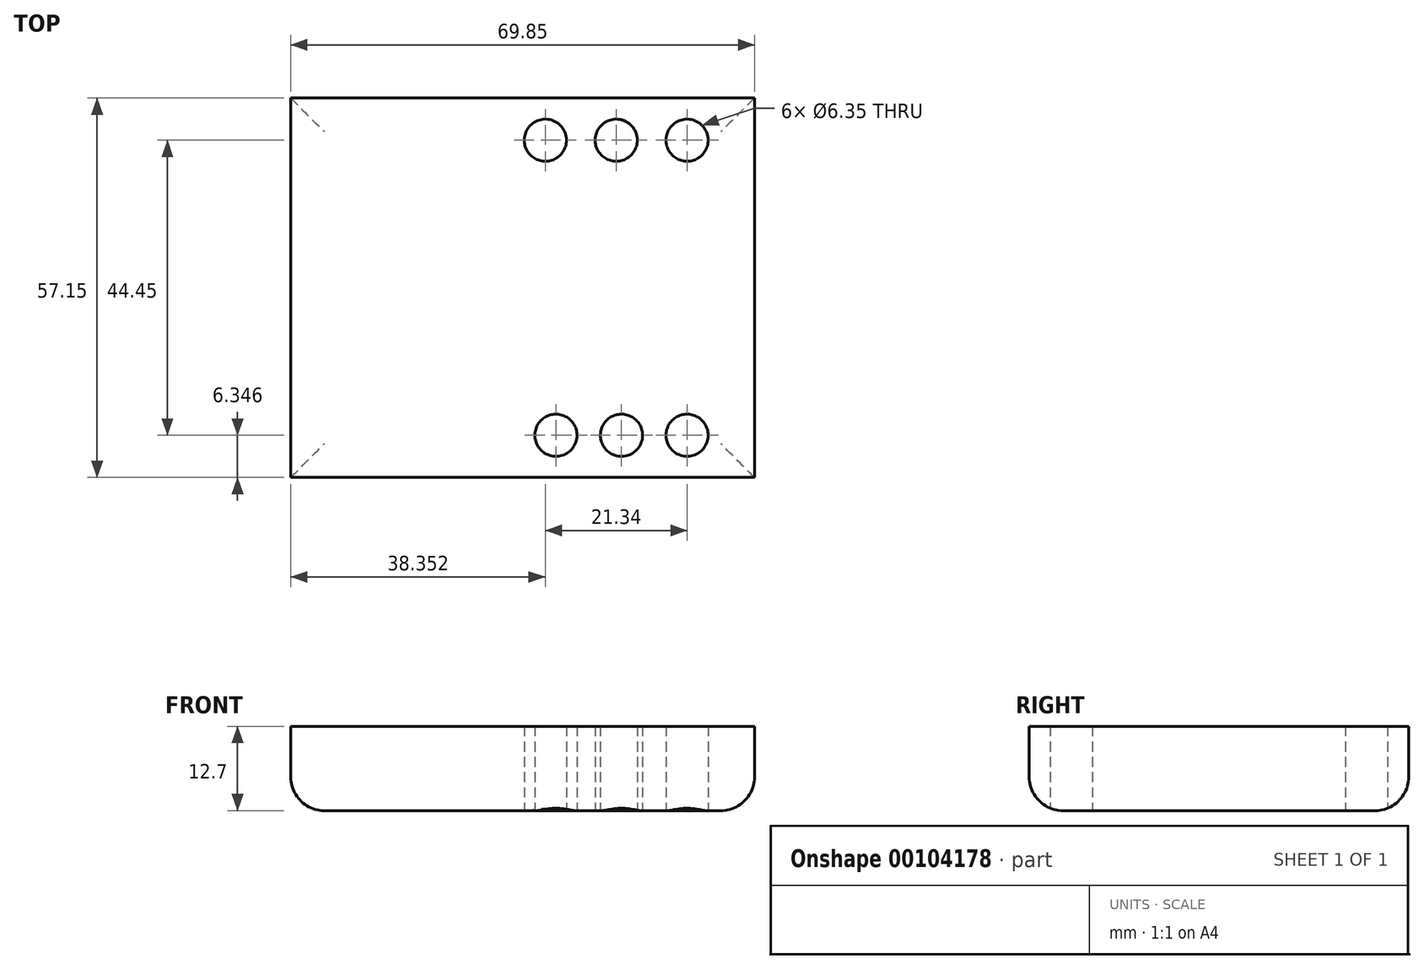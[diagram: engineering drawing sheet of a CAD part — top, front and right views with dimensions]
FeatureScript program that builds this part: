
annotation { "Feature Type Name" : "Feature", "Feature Type Description" : "" }
export const myFeature = defineFeature(function(context is Context, id is Id, definition is map)
    precondition{}
    {
        {
            var Q0;
            Q0=qCreatedBy(makeId("Top.planeOp"),FACE);
            var sketch = newSketch(context, id + "F0", { "sketchPlane" : qUnion([Q0])});
            skLineSegment(sketch, "E0.bottom", {"start": v(-35.88, 40.53) * mm, "end": v(33.97, 40.53) * mm});
            skLineSegment(sketch, "E0.top", {"start": v(-35.88, -16.62) * mm, "end": v(33.97, -16.62) * mm});
            skLineSegment(sketch, "E0.left", {"start": v(-35.88, 40.53) * mm, "end": v(-35.88, -16.62) * mm});
            skLineSegment(sketch, "E0.right", {"start": v(33.97, 40.53) * mm, "end": v(33.97, -16.62) * mm});
            skCircle(sketch, "E1", {"center": v(23.81, -10.27) * mm, "radius": 3.18 * mm});
            skLineSegment(sketch, "E2", {"start": v(23.81, -10.27) * mm, "end": v(4.07, -10.27) * mm});
            skCircle(sketch, "E3", {"center": v(4.07, -10.27) * mm, "radius": 3.18 * mm});
            skCircle(sketch, "E4", {"center": v(13.94, -10.27) * mm, "radius": 3.18 * mm});
            skLineSegment(sketch, "E5", {"start": v(23.81, 34.18) * mm, "end": v(2.47, 34.18) * mm});
            skCircle(sketch, "E6", {"center": v(23.81, 34.18) * mm, "radius": 3.18 * mm});
            skCircle(sketch, "E7", {"center": v(13.14, 34.18) * mm, "radius": 3.18 * mm});
            skCircle(sketch, "E8", {"center": v(2.47, 34.18) * mm, "radius": 3.18 * mm});
            skLineSegment(sketch, "E9", {"start": v(23.81, -10.27) * mm, "end": v(23.81, -16.62) * mm});
            skLineSegment(sketch, "E10", {"start": v(23.81, -10.27) * mm, "end": v(33.97, -10.27) * mm});
            skLineSegment(sketch, "E11", {"start": v(23.81, 34.18) * mm, "end": v(33.97, 34.18) * mm});
            skLineSegment(sketch, "E12", {"start": v(23.81, 34.18) * mm, "end": v(23.81, 40.53) * mm});
            skSolve(sketch);
        }
        {
            var Q0;
            {var subQ16=sQuery(id+"F0.wireOp",EDGE,"E0.left");Q0=makeQuery(id+"F0.imprint","IMPRINT",FACE,{"disambiguationData":[TD([[makeQuery(id+"F0.imprint","IMPRINT",EDGE,{"derivedFrom":subQ16}),1.0]])]});}
            var Q1;
            {var subQ1=sQuery(id+"F0.wireOp",EDGE,"E0.right");var subQ5=sQuery(id+"F0.wireOp",EDGE,"E0.bottom");var subQ6=makeQuery(id+"F0.imprint","INTERSECT",VERTEX,{"derivedFrom":[subQ5,subQ1]});Q1=makeQuery(id+"F0.imprint","IMPRINT",FACE,{"disambiguationData":[TD([[makeQuery(id+"F0.imprint","IMPRINT",EDGE,{"disambiguationData":[TD([[subQ6,1.0]])],"derivedFrom":subQ5}),-1.0]])]});}
            var Q2;
            {var subQ1=sQuery(id+"F0.wireOp",EDGE,"E0.top");var subQ5=sQuery(id+"F0.wireOp",EDGE,"E0.right");var subQ6=makeQuery(id+"F0.imprint","INTERSECT",VERTEX,{"derivedFrom":[subQ1,subQ5]});Q2=makeQuery(id+"F0.imprint","IMPRINT",FACE,{"disambiguationData":[TD([[makeQuery(id+"F0.imprint","IMPRINT",EDGE,{"disambiguationData":[TD([[subQ6,1.0]])],"derivedFrom":subQ1}),1.0]])]});}
            extrude(context, id + "F1", {"entities" : qUnion([Q0, Q1, Q2]), "depth" : 12.7 * mm});
        }
        {
            var Q0;
            Q0=makeQuery(id+"F1.opExtrude","CAP_EDGE",EDGE,{"disambiguationData":[OSD([sQuery(id+"F0.wireOp",EDGE,"E0.top")])],"isStart":true});
            var Q1;
            Q1=makeQuery(id+"F1.opExtrude","CAP_EDGE",EDGE,{"disambiguationData":[OSD([sQuery(id+"F0.wireOp",EDGE,"E0.right")])],"isStart":true});
            var Q2;
            Q2=makeQuery(id+"F1.opExtrude","CAP_EDGE",EDGE,{"disambiguationData":[OSD([sQuery(id+"F0.wireOp",EDGE,"E0.bottom")])],"isStart":true});
            var Q3;
            Q3=makeQuery(id+"F1.opExtrude","CAP_EDGE",EDGE,{"disambiguationData":[OSD([sQuery(id+"F0.wireOp",EDGE,"E0.left")])],"isStart":true});
            fillet(context, id + "F2", {"entities" : qUnion([Q0, Q1, Q2, Q3]), "radius" : 5.08 * mm, "tangentPropagation" : true, "allowEdgeOverflow" : false});
        }
    });
